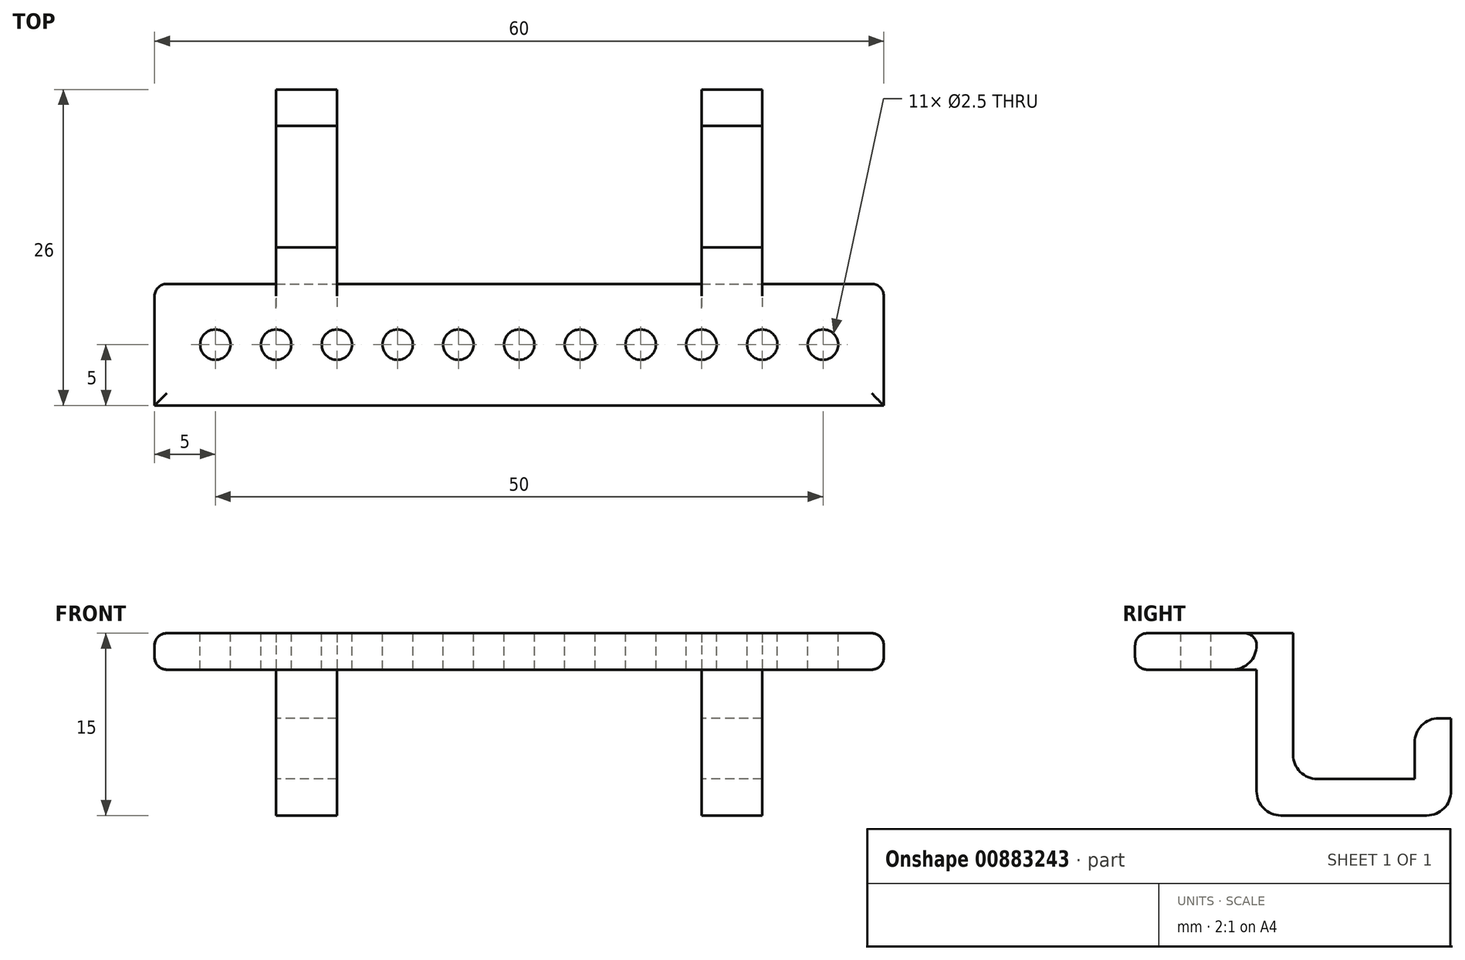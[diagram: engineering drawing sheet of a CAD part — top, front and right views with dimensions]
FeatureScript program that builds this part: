
annotation { "Feature Type Name" : "Feature", "Feature Type Description" : "" }
export const myFeature = defineFeature(function(context is Context, id is Id, definition is map)
    precondition{}
    {
        {
            var Q0;
            Q0=qCreatedBy(makeId("Top.planeOp"),FACE);
            var sketch = newSketch(context, id + "F0", { "sketchPlane" : qUnion([Q0])});
            skLineSegment(sketch, "E0.bottom", {"start": v(-30, 5) * mm, "end": v(30, 5) * mm});
            skLineSegment(sketch, "E0.top", {"start": v(-30, -5) * mm, "end": v(30, -5) * mm});
            skLineSegment(sketch, "E0.left", {"start": v(-30, 5) * mm, "end": v(-30, -5) * mm});
            skLineSegment(sketch, "E0.right", {"start": v(30, 5) * mm, "end": v(30, -5) * mm});
            skSolve(sketch);
        }
        {
            var Q0;
            Q0 = qSketchRegion(id + "F0", true);
            extrude(context, id + "F1", {"entities" : qUnion([Q0]), "depth" : 3 * mm, "offsetDistance" : 25 * mm});
        }
        {
            var Q0;
            Q0=makeQuery(id+"F1.opExtrude","CAP_FACE",FACE,{"disambiguationData":[OSD([sQuery(id+"F0.wireOp",EDGE,"E0.bottom"),sQuery(id+"F0.wireOp",EDGE,"E0.top"),sQuery(id+"F0.wireOp",EDGE,"E0.left"),sQuery(id+"F0.wireOp",EDGE,"E0.right")])],"isStart":false});
            var sketch = newSketch(context, id + "F2", { "sketchPlane" : qUnion([Q0])});
            skLineSegment(sketch, "E1", {"start": v(-30, 0) * mm, "end": v(30, 0) * mm, "construction": true});
            skCircle(sketch, "E2", {"center": v(-25, 0) * mm, "radius": 1.25 * mm});
            skCircle(sketch, "E3.1.0.0", {"center": v(-20, 0) * mm, "radius": 1.25 * mm});
            skCircle(sketch, "E3.2.0.0", {"center": v(-15, 0) * mm, "radius": 1.25 * mm});
            skCircle(sketch, "E3.3.0.0", {"center": v(-10, 0) * mm, "radius": 1.25 * mm});
            skCircle(sketch, "E3.4.0.0", {"center": v(-5, 0) * mm, "radius": 1.25 * mm});
            skCircle(sketch, "E3.5.0.0", {"center": v(0, 0) * mm, "radius": 1.25 * mm});
            skCircle(sketch, "E3.6.0.0", {"center": v(5, 0) * mm, "radius": 1.25 * mm});
            skCircle(sketch, "E3.7.0.0", {"center": v(10, 0) * mm, "radius": 1.25 * mm});
            skCircle(sketch, "E3.8.0.0", {"center": v(15, 0) * mm, "radius": 1.25 * mm});
            skCircle(sketch, "E3.9.0.0", {"center": v(20, 0) * mm, "radius": 1.25 * mm});
            skLineSegment(sketch, "E3.direction1", {"start": v(-25, 0) * mm, "end": v(-20, 0) * mm, "construction": true});
            skCircle(sketch, "E4.0.10.0", {"center": v(25, 0) * mm, "radius": 1.25 * mm});
            skSolve(sketch);
        }
        {
            var Q0;
            Q0 = qSketchRegion(id + "F2", true);
            extrude(context, id + "F3", {"entities" : qUnion([Q0]), "operationType" : NewBodyOperationType.REMOVE, "oppositeDirection" : true, "depth" : 3 * mm, "offsetDistance" : 25 * mm});
        }
        {
            var Q0;
            Q0=makeQuery(id+"F1.opExtrude","SWEPT_FACE",FACE,{"disambiguationData":[OSD([sQuery(id+"F0.wireOp",EDGE,"E0.bottom")])]});
            var sketch = newSketch(context, id + "F4", { "sketchPlane" : qUnion([Q0])});
            skLineSegment(sketch, "E5.bottom", {"start": v(20, 3) * mm, "end": v(15, 3) * mm});
            skLineSegment(sketch, "E5.top", {"start": v(20, -12) * mm, "end": v(15, -12) * mm});
            skLineSegment(sketch, "E5.left", {"start": v(20, 3) * mm, "end": v(20, -12) * mm});
            skLineSegment(sketch, "E5.right", {"start": v(15, 3) * mm, "end": v(15, -12) * mm});
            skLineSegment(sketch, "E6", {"start": v(0, 0) * mm, "end": v(0, 3) * mm, "construction": true});
            skLineSegment(sketch, "E7.MirrorCS", {"start": v(-20, -12) * mm, "end": v(-15, -12) * mm});
            skLineSegment(sketch, "E8.MirrorCS", {"start": v(-20, 3) * mm, "end": v(-20, -12) * mm});
            skLineSegment(sketch, "E9.MirrorCS", {"start": v(-20, 3) * mm, "end": v(-15, 3) * mm});
            skLineSegment(sketch, "E10.MirrorCS", {"start": v(-15, 3) * mm, "end": v(-15, -12) * mm});
            skSolve(sketch);
        }
        {
            var Q0;
            Q0 = qSketchRegion(id + "F4", true);
            extrude(context, id + "F5", {"entities" : qUnion([Q0]), "operationType" : NewBodyOperationType.ADD, "depth" : 16 * mm, "offsetDistance" : 25 * mm});
        }
        {
            var Q0;
            Q0=makeQuery(id+"F5.opExtrude","SWEPT_FACE",FACE,{"disambiguationData":[OSD([sQuery(id+"F4.wireOp",EDGE,"E5.left")])]});
            var sketch = newSketch(context, id + "F6", { "sketchPlane" : qUnion([Q0])});
            skLineSegment(sketch, "E11", {"start": v(-8, 3) * mm, "end": v(-8, -9) * mm});
            skLineSegment(sketch, "E12", {"start": v(-8, -9) * mm, "end": v(-18, -9) * mm});
            skLineSegment(sketch, "E13", {"start": v(-18, -9) * mm, "end": v(-18, -4) * mm});
            skLineSegment(sketch, "E14", {"start": v(-18, -4) * mm, "end": v(-21, -4) * mm});
            skLineSegment(sketch, "E15", {"start": v(-21, -4) * mm, "end": v(-21, 3) * mm});
            skLineSegment(sketch, "E16", {"start": v(-21, 3) * mm, "end": v(-8, 3) * mm});
            skSolve(sketch);
        }
        {
            var Q0;
            Q0 = qSketchRegion(id + "F6", true);
            extrude(context, id + "F7", {"entities" : qUnion([Q0]), "operationType" : NewBodyOperationType.REMOVE, "oppositeDirection" : true, "depth" : 60 * mm, "offsetDistance" : 25 * mm});
        }
        {
            var Q0;
            {var subQ0=sQuery(id+"F0.wireOp",EDGE,"E0.bottom");Q0=makeQuery(id+"F5.boolean.opBoolean","SPLIT",EDGE,{"disambiguationData":[topologyDisambiguationEdgeConnected([makeQuery(id+"F1.opExtrude","CAP_FACE",FACE,{"disambiguationData":[OSD([subQ0,sQuery(id+"F0.wireOp",EDGE,"E0.top"),sQuery(id+"F0.wireOp",EDGE,"E0.left"),sQuery(id+"F0.wireOp",EDGE,"E0.right")])],"isStart":true}),makeQuery(id+"F5.opExtrude","CAP_FACE",FACE,{"disambiguationData":[OSD([sQuery(id+"F4.wireOp",EDGE,"E5.bottom"),sQuery(id+"F4.wireOp",EDGE,"E5.top"),sQuery(id+"F4.wireOp",EDGE,"E5.left"),sQuery(id+"F4.wireOp",EDGE,"E5.right")])],"isStart":true})])],"derivedFrom":makeQuery(id+"F1.opExtrude","CAP_EDGE",EDGE,{"disambiguationData":[OSD([subQ0])],"isStart":true})});}
            var Q1;
            {var subQ0=sQuery(id+"F0.wireOp",EDGE,"E0.bottom");Q1=makeQuery(id+"F5.boolean.opBoolean","SPLIT",EDGE,{"disambiguationData":[topologyDisambiguationEdgeConnected([makeQuery(id+"F1.opExtrude","CAP_FACE",FACE,{"disambiguationData":[OSD([subQ0,sQuery(id+"F0.wireOp",EDGE,"E0.top"),sQuery(id+"F0.wireOp",EDGE,"E0.left"),sQuery(id+"F0.wireOp",EDGE,"E0.right")])],"isStart":true}),makeQuery(id+"F5.opExtrude","CAP_FACE",FACE,{"disambiguationData":[OSD([sQuery(id+"F4.wireOp",EDGE,"E7.MirrorCS"),sQuery(id+"F4.wireOp",EDGE,"E8.MirrorCS"),sQuery(id+"F4.wireOp",EDGE,"E9.MirrorCS"),sQuery(id+"F4.wireOp",EDGE,"E10.MirrorCS")])],"isStart":true})])],"derivedFrom":makeQuery(id+"F1.opExtrude","CAP_EDGE",EDGE,{"disambiguationData":[OSD([subQ0])],"isStart":true})});}
            var Q2;
            Q2=makeQuery(id+"F5.opExtrude","CAP_EDGE",EDGE,{"disambiguationData":[OSD([sQuery(id+"F4.wireOp",EDGE,"E5.top")])],"isStart":true});
            var Q3;
            Q3=makeQuery(id+"F5.opExtrude","CAP_EDGE",EDGE,{"disambiguationData":[OSD([sQuery(id+"F4.wireOp",EDGE,"E7.MirrorCS")])],"isStart":true});
            var Q4;
            Q4=makeQuery(id+"F5.opExtrude","CAP_EDGE",EDGE,{"disambiguationData":[OSD([sQuery(id+"F4.wireOp",EDGE,"E5.top")])],"isStart":false});
            var Q5;
            Q5=makeQuery(id+"F5.opExtrude","CAP_EDGE",EDGE,{"disambiguationData":[OSD([sQuery(id+"F4.wireOp",EDGE,"E7.MirrorCS")])],"isStart":false});
            var Q6;
            {var subQ0=sQuery(id+"F4.wireOp",EDGE,"E5.left");var subQ1=sQuery(id+"F6.wireOp",EDGE,"E14");Q6=makeQuery(id+"F7.boolean.opBoolean","COPY",EDGE,{"disambiguationData":[topologyDisambiguationEdgeConnected([makeQuery(id+"F5.opExtrude","CAP_FACE",FACE,{"disambiguationData":[OSD([sQuery(id+"F4.wireOp",EDGE,"E5.bottom"),sQuery(id+"F4.wireOp",EDGE,"E5.top"),subQ0,sQuery(id+"F4.wireOp",EDGE,"E5.right")])],"isStart":false})])],"derivedFrom":makeQuery(id+"F7.opExtrude","SWEPT_EDGE",EDGE,{"disambiguationData":[OSD([subQ0,subQ1,sQuery(id+"F6.wireOp",EDGE,"E15")])]})});}
            var Q7;
            {var subQ0=sQuery(id+"F6.wireOp",EDGE,"E14");Q7=makeQuery(id+"F7.boolean.opBoolean","COPY",EDGE,{"disambiguationData":[topologyDisambiguationEdgeConnected([makeQuery(id+"F5.opExtrude","CAP_FACE",FACE,{"disambiguationData":[OSD([sQuery(id+"F4.wireOp",EDGE,"E7.MirrorCS"),sQuery(id+"F4.wireOp",EDGE,"E8.MirrorCS"),sQuery(id+"F4.wireOp",EDGE,"E9.MirrorCS"),sQuery(id+"F4.wireOp",EDGE,"E10.MirrorCS")])],"isStart":false})])],"derivedFrom":makeQuery(id+"F7.opExtrude","SWEPT_EDGE",EDGE,{"disambiguationData":[OSD([sQuery(id+"F4.wireOp",EDGE,"E5.left"),subQ0,sQuery(id+"F6.wireOp",EDGE,"E15")])]})});}
            var Q8;
            {var subQ0=sQuery(id+"F6.wireOp",EDGE,"E14");var subQ1=sQuery(id+"F6.wireOp",EDGE,"E13");Q8=makeQuery(id+"F7.boolean.opBoolean","COPY",EDGE,{"disambiguationData":[TD([makeQuery(id+"F5.opExtrude","SWEPT_FACE",FACE,{"disambiguationData":[OSD([sQuery(id+"F4.wireOp",EDGE,"E5.left")])]})])],"derivedFrom":makeQuery(id+"F7.opExtrude","SWEPT_EDGE",EDGE,{"disambiguationData":[OSD([subQ1,subQ0])]})});}
            var Q9;
            {var subQ0=sQuery(id+"F6.wireOp",EDGE,"E14");var subQ1=sQuery(id+"F6.wireOp",EDGE,"E13");Q9=makeQuery(id+"F7.boolean.opBoolean","COPY",EDGE,{"disambiguationData":[TD([makeQuery(id+"F5.opExtrude","SWEPT_FACE",FACE,{"disambiguationData":[OSD([sQuery(id+"F4.wireOp",EDGE,"E8.MirrorCS")])]})])],"derivedFrom":makeQuery(id+"F7.opExtrude","SWEPT_EDGE",EDGE,{"disambiguationData":[OSD([subQ1,subQ0])]})});}
            var Q10;
            {var subQ0=sQuery(id+"F4.wireOp",EDGE,"E5.bottom");var subQ1=sQuery(id+"F0.wireOp",EDGE,"E0.bottom");var subQ2=sQuery(id+"F6.wireOp",EDGE,"E11");Q10=makeQuery(id+"F7.boolean.opBoolean","COPY",EDGE,{"disambiguationData":[TD([makeQuery(id+"F5.opExtrude","SWEPT_FACE",FACE,{"disambiguationData":[OSD([sQuery(id+"F4.wireOp",EDGE,"E8.MirrorCS")])]})])],"derivedFrom":makeQuery(id+"F7.opExtrude","SWEPT_EDGE",EDGE,{"disambiguationData":[OSD([subQ1,subQ0,sQuery(id+"F4.wireOp",EDGE,"E5.left"),subQ2,sQuery(id+"F6.wireOp",EDGE,"E16")])]})});}
            var Q11;
            {var subQ0=sQuery(id+"F6.wireOp",EDGE,"E11");var subQ1=sQuery(id+"F4.wireOp",EDGE,"E5.bottom");var subQ2=sQuery(id+"F4.wireOp",EDGE,"E5.left");var subQ3=sQuery(id+"F0.wireOp",EDGE,"E0.bottom");Q11=makeQuery(id+"F7.boolean.opBoolean","COPY",EDGE,{"disambiguationData":[TD([makeQuery(id+"F5.opExtrude","SWEPT_FACE",FACE,{"disambiguationData":[OSD([subQ2])]})])],"derivedFrom":makeQuery(id+"F7.opExtrude","SWEPT_EDGE",EDGE,{"disambiguationData":[OSD([subQ3,subQ1,subQ2,subQ0,sQuery(id+"F6.wireOp",EDGE,"E16")])]})});}
            var Q12;
            {var subQ0=sQuery(id+"F6.wireOp",EDGE,"E11");var subQ1=sQuery(id+"F6.wireOp",EDGE,"E12");Q12=makeQuery(id+"F7.boolean.opBoolean","COPY",EDGE,{"disambiguationData":[TD([makeQuery(id+"F5.opExtrude","SWEPT_FACE",FACE,{"disambiguationData":[OSD([sQuery(id+"F4.wireOp",EDGE,"E8.MirrorCS")])]})])],"derivedFrom":makeQuery(id+"F7.opExtrude","SWEPT_EDGE",EDGE,{"disambiguationData":[OSD([subQ0,subQ1])]})});}
            var Q13;
            {var subQ0=sQuery(id+"F6.wireOp",EDGE,"E11");var subQ1=sQuery(id+"F6.wireOp",EDGE,"E12");Q13=makeQuery(id+"F7.boolean.opBoolean","COPY",EDGE,{"disambiguationData":[TD([makeQuery(id+"F5.opExtrude","SWEPT_FACE",FACE,{"disambiguationData":[OSD([sQuery(id+"F4.wireOp",EDGE,"E5.left")])]})])],"derivedFrom":makeQuery(id+"F7.opExtrude","SWEPT_EDGE",EDGE,{"disambiguationData":[OSD([subQ0,subQ1])]})});}
            fillet(context, id + "F8", {"entities" : qUnion([Q0, Q1, Q2, Q3, Q4, Q5, Q6, Q7, Q8, Q9, Q10, Q11, Q12, Q13]), "radius" : 2 * mm, "tangentPropagation" : true, "allowEdgeOverflow" : false});
        }
        {
            var Q0;
            Q0=makeQuery(id+"F1.opExtrude","CAP_EDGE",EDGE,{"disambiguationData":[OSD([sQuery(id+"F0.wireOp",EDGE,"E0.top")])],"isStart":false});
            var Q1;
            Q1=makeQuery(id+"F1.opExtrude","CAP_EDGE",EDGE,{"disambiguationData":[OSD([sQuery(id+"F0.wireOp",EDGE,"E0.right")])],"isStart":false});
            var Q2;
            {var subQ0=sQuery(id+"F0.wireOp",EDGE,"E0.right");var subQ1=sQuery(id+"F0.wireOp",EDGE,"E0.bottom");Q2=makeQuery(id+"F5.boolean.opBoolean","SPLIT",EDGE,{"disambiguationData":[TD([makeQuery(id+"F1.opExtrude","SWEPT_FACE",FACE,{"disambiguationData":[OSD([subQ0])]})])],"derivedFrom":makeQuery(id+"F1.opExtrude","CAP_EDGE",EDGE,{"disambiguationData":[OSD([subQ1])],"isStart":false})});}
            var Q3;
            {var subQ0=sQuery(id+"F0.wireOp",EDGE,"E0.bottom");Q3=makeQuery(id+"F5.boolean.opBoolean","SPLIT",EDGE,{"disambiguationData":[TD([makeQuery(id+"F5.opExtrude","SWEPT_FACE",FACE,{"disambiguationData":[OSD([sQuery(id+"F4.wireOp",EDGE,"E5.right")])]})])],"derivedFrom":makeQuery(id+"F1.opExtrude","CAP_EDGE",EDGE,{"disambiguationData":[OSD([subQ0])],"isStart":false})});}
            var Q4;
            {var subQ0=sQuery(id+"F0.wireOp",EDGE,"E0.left");var subQ1=sQuery(id+"F0.wireOp",EDGE,"E0.bottom");Q4=makeQuery(id+"F5.boolean.opBoolean","SPLIT",EDGE,{"disambiguationData":[TD([makeQuery(id+"F1.opExtrude","SWEPT_FACE",FACE,{"disambiguationData":[OSD([subQ0])]})])],"derivedFrom":makeQuery(id+"F1.opExtrude","CAP_EDGE",EDGE,{"disambiguationData":[OSD([subQ1])],"isStart":false})});}
            var Q5;
            Q5=makeQuery(id+"F1.opExtrude","CAP_EDGE",EDGE,{"disambiguationData":[OSD([sQuery(id+"F0.wireOp",EDGE,"E0.left")])],"isStart":false});
            var Q6;
            Q6=makeQuery(id+"F1.opExtrude","CAP_EDGE",EDGE,{"disambiguationData":[OSD([sQuery(id+"F0.wireOp",EDGE,"E0.top")])],"isStart":true});
            var Q7;
            Q7=makeQuery(id+"F1.opExtrude","CAP_EDGE",EDGE,{"disambiguationData":[OSD([sQuery(id+"F0.wireOp",EDGE,"E0.right")])],"isStart":true});
            var Q8;
            {var subQ0=sQuery(id+"F0.wireOp",EDGE,"E0.right");var subQ1=sQuery(id+"F0.wireOp",EDGE,"E0.bottom");var subQ2=makeQuery(id+"F1.opExtrude","CAP_FACE",FACE,{"disambiguationData":[OSD([subQ1,sQuery(id+"F0.wireOp",EDGE,"E0.top"),sQuery(id+"F0.wireOp",EDGE,"E0.left"),subQ0])],"isStart":true});var subQ4=makeQuery(id+"F1.opExtrude","SWEPT_FACE",FACE,{"disambiguationData":[OSD([subQ1])]});Q8=makeQuery(id+"F5.boolean.opBoolean","SPLIT",EDGE,{"disambiguationData":[topologyDisambiguationEdgeConnected([subQ4,subQ2]),TD([makeQuery(id+"F1.opExtrude","SWEPT_FACE",FACE,{"disambiguationData":[OSD([subQ0])]})])],"derivedFrom":makeQuery(id+"F1.opExtrude","CAP_EDGE",EDGE,{"disambiguationData":[OSD([subQ1])],"isStart":true})});}
            var Q9;
            {var subQ0=sQuery(id+"F4.wireOp",EDGE,"E5.right");var subQ1=sQuery(id+"F0.wireOp",EDGE,"E0.bottom");var subQ2=makeQuery(id+"F1.opExtrude","SWEPT_FACE",FACE,{"disambiguationData":[OSD([subQ1])]});var subQ3=makeQuery(id+"F1.opExtrude","CAP_FACE",FACE,{"disambiguationData":[OSD([subQ1,sQuery(id+"F0.wireOp",EDGE,"E0.top"),sQuery(id+"F0.wireOp",EDGE,"E0.left"),sQuery(id+"F0.wireOp",EDGE,"E0.right")])],"isStart":true});Q9=makeQuery(id+"F5.boolean.opBoolean","SPLIT",EDGE,{"disambiguationData":[topologyDisambiguationEdgeConnected([subQ2,subQ3]),TD([makeQuery(id+"F5.opExtrude","SWEPT_FACE",FACE,{"disambiguationData":[OSD([subQ0])]})])],"derivedFrom":makeQuery(id+"F1.opExtrude","CAP_EDGE",EDGE,{"disambiguationData":[OSD([subQ1])],"isStart":true})});}
            var Q10;
            {var subQ1=sQuery(id+"F0.wireOp",EDGE,"E0.bottom");var subQ2=makeQuery(id+"F1.opExtrude","SWEPT_FACE",FACE,{"disambiguationData":[OSD([subQ1])]});var subQ3=sQuery(id+"F0.wireOp",EDGE,"E0.left");var subQ4=makeQuery(id+"F1.opExtrude","CAP_FACE",FACE,{"disambiguationData":[OSD([subQ1,sQuery(id+"F0.wireOp",EDGE,"E0.top"),subQ3,sQuery(id+"F0.wireOp",EDGE,"E0.right")])],"isStart":true});Q10=makeQuery(id+"F5.boolean.opBoolean","SPLIT",EDGE,{"disambiguationData":[topologyDisambiguationEdgeConnected([subQ2,subQ4]),TD([makeQuery(id+"F1.opExtrude","SWEPT_FACE",FACE,{"disambiguationData":[OSD([subQ3])]})])],"derivedFrom":makeQuery(id+"F1.opExtrude","CAP_EDGE",EDGE,{"disambiguationData":[OSD([subQ1])],"isStart":true})});}
            var Q11;
            Q11=makeQuery(id+"F1.opExtrude","CAP_EDGE",EDGE,{"disambiguationData":[OSD([sQuery(id+"F0.wireOp",EDGE,"E0.left")])],"isStart":true});
            fillet(context, id + "F9", {"entities" : qUnion([Q0, Q1, Q2, Q3, Q4, Q5, Q6, Q7, Q8, Q9, Q10, Q11]), "radius" : 1 * mm, "tangentPropagation" : true, "allowEdgeOverflow" : false});
        }
    });
